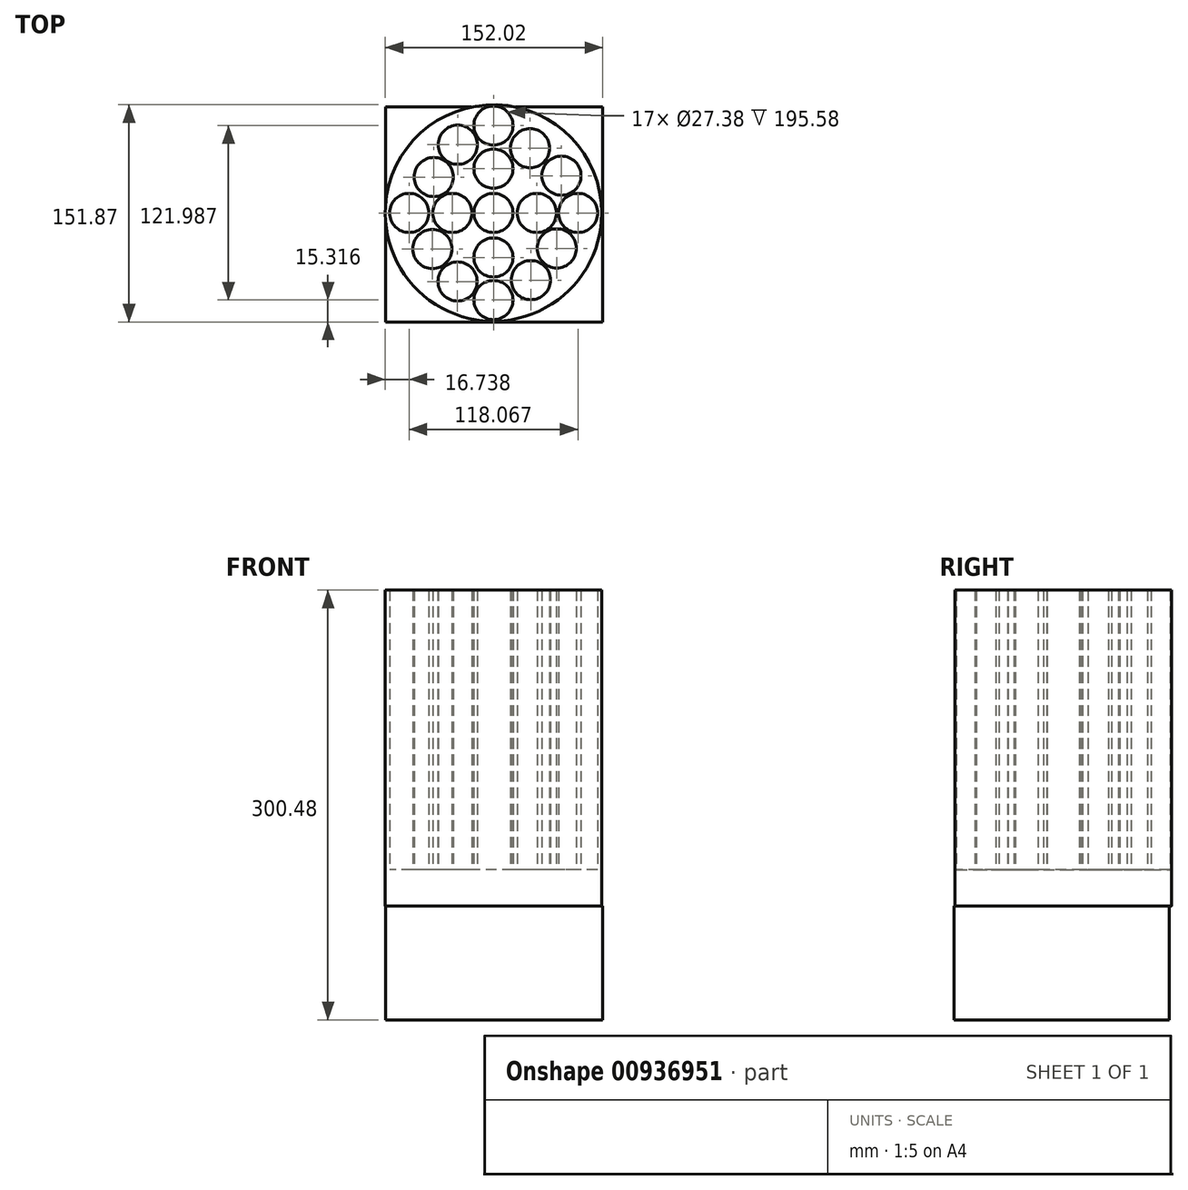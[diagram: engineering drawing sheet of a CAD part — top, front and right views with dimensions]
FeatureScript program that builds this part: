
annotation { "Feature Type Name" : "Feature", "Feature Type Description" : "" }
export const myFeature = defineFeature(function(context is Context, id is Id, definition is map)
    precondition{}
    {
        {
            var Q0;
            Q0=qCreatedBy(makeId("Top.planeOp"),FACE);
            var sketch = newSketch(context, id + "F0", { "sketchPlane" : qUnion([Q0])});
            skCircle(sketch, "E0", {"center": v(0, 0) * mm, "radius": 75.66 * mm});
            skSolve(sketch);
        }
        {
            var Q0;
            Q0=makeQuery(id+"F0.imprint","IMPRINT",FACE,{"disambiguationData":[TD([[makeQuery(id+"F0.imprint","IMPRINT",EDGE,{"derivedFrom":sQuery(id+"F0.wireOp",EDGE,"E0")}),1.0]])]});
            extrude(context, id + "F1", {"entities" : qUnion([Q0]), "depth" : 25.4 * mm, "offsetDistance" : 25.4 * mm});
        }
        {
            var Q0;
            Q0=makeQuery(id+"F1.opExtrude","CAP_FACE",FACE,{"disambiguationData":[OSD([sQuery(id+"F0.wireOp",EDGE,"E0")])],"isStart":false});
            var sketch = newSketch(context, id + "F2", { "sketchPlane" : qUnion([Q0])});
            skCircle(sketch, "E1", {"center": v(-58.92, 0) * mm, "radius": 13.69 * mm});
            skCircle(sketch, "E2", {"center": v(-28.7, 0) * mm, "radius": 13.69 * mm});
            skCircle(sketch, "E3", {"center": v(59.14, 0) * mm, "radius": 13.69 * mm});
            skCircle(sketch, "E4", {"center": v(30.38, 0) * mm, "radius": 13.69 * mm});
            skCircle(sketch, "E5", {"center": v(0, 0) * mm, "radius": 13.69 * mm});
            skCircle(sketch, "E6", {"center": v(0, 61.1) * mm, "radius": 13.69 * mm});
            skCircle(sketch, "E7", {"center": v(0, 30.98) * mm, "radius": 13.69 * mm});
            skCircle(sketch, "E8", {"center": v(0, -31.11) * mm, "radius": 13.69 * mm});
            skCircle(sketch, "E9", {"center": v(0, -60.9) * mm, "radius": 13.69 * mm});
            skCircle(sketch, "E10", {"center": v(26.14, -46.98) * mm, "radius": 13.69 * mm});
            skCircle(sketch, "E11", {"center": v(44.3, -24.78) * mm, "radius": 13.69 * mm});
            skCircle(sketch, "E12", {"center": v(-42.73, -25.17) * mm, "radius": 13.69 * mm});
            skCircle(sketch, "E13", {"center": v(-25.13, -47.92) * mm, "radius": 13.69 * mm});
            skCircle(sketch, "E14", {"center": v(-41.72, 25.13) * mm, "radius": 13.69 * mm});
            skCircle(sketch, "E15", {"center": v(-24.92, 47.71) * mm, "radius": 13.69 * mm});
            skCircle(sketch, "E16", {"center": v(25.62, 45.29) * mm, "radius": 13.69 * mm});
            skCircle(sketch, "E17", {"center": v(47.56, 26.05) * mm, "radius": 13.69 * mm});
            skSolve(sketch);
        }
        {
            var Q0;
            Q0=makeQuery(id+"F2.imprint","IMPRINT",FACE,{"disambiguationData":[TD([[makeQuery(id+"F2.imprint","IMPRINT",EDGE,{"derivedFrom":sQuery(id+"F2.wireOp",EDGE,"E1")}),-1.0]])]});
            extrude(context, id + "F3", {"entities" : qUnion([Q0]), "operationType" : NewBodyOperationType.ADD, "depth" : 195.58 * mm, "offsetDistance" : 25.4 * mm});
        }
        {
            var Q0;
            Q0=qCreatedBy(makeId("Top.planeOp"),FACE);
            var sketch = newSketch(context, id + "F4", { "sketchPlane" : qUnion([Q0])});
            skLineSegment(sketch, "E18.bottom", {"start": v(-75.51, -76.21) * mm, "end": v(76.36, -76.21) * mm});
            skLineSegment(sketch, "E18.top", {"start": v(-75.51, 74.07) * mm, "end": v(76.36, 74.07) * mm});
            skLineSegment(sketch, "E18.left", {"start": v(-75.51, -76.21) * mm, "end": v(-75.51, 74.07) * mm});
            skLineSegment(sketch, "E18.right", {"start": v(76.36, -76.21) * mm, "end": v(76.36, 74.07) * mm});
            skSolve(sketch);
        }
        {
            var Q0;
            Q0=makeQuery(id+"F4.imprint","IMPRINT",FACE,{"disambiguationData":[TD([[makeQuery(id+"F4.imprint","IMPRINT",EDGE,{"derivedFrom":sQuery(id+"F4.wireOp",EDGE,"E18.bottom")}),1.0]])]});
            extrude(context, id + "F5", {"entities" : qUnion([Q0]), "operationType" : NewBodyOperationType.ADD, "oppositeDirection" : true, "depth" : 79.5 * mm, "offsetDistance" : 25.4 * mm});
        }
    });
